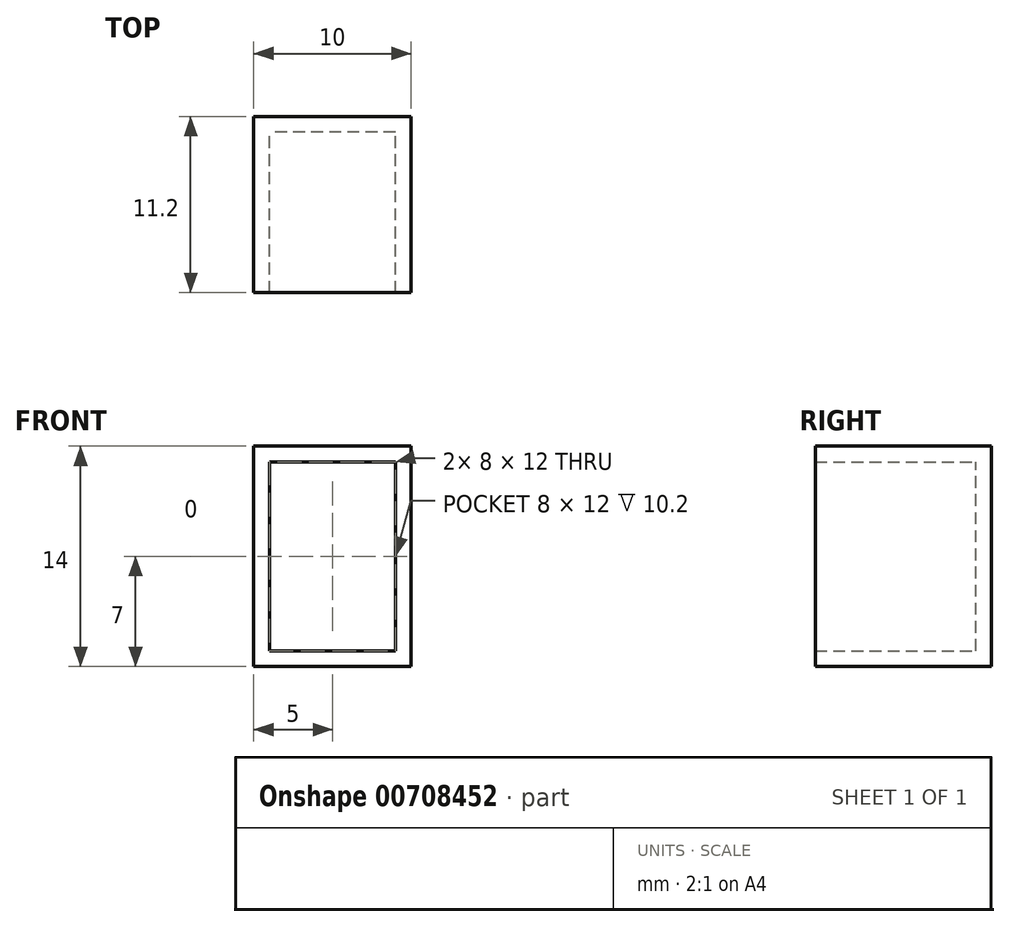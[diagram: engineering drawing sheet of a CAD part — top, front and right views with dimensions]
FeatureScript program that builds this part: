
annotation { "Feature Type Name" : "Feature", "Feature Type Description" : "" }
export const myFeature = defineFeature(function(context is Context, id is Id, definition is map)
    precondition{}
    {
        {
            var Q0;
            Q0=qCreatedBy(makeId("Front.planeOp"),FACE);
            var sketch = newSketch(context, id + "F0", { "sketchPlane" : qUnion([Q0])});
            skLineSegment(sketch, "E0", {"start": v(0, 0) * mm, "end": v(0, 14) * mm});
            skLineSegment(sketch, "E1", {"start": v(0, 14) * mm, "end": v(10, 14) * mm});
            skLineSegment(sketch, "E2", {"start": v(10, 14) * mm, "end": v(10, 0) * mm});
            skLineSegment(sketch, "E3", {"start": v(10, 0) * mm, "end": v(0, 0) * mm});
            skSolve(sketch);
        }
        {
            var Q0;
            Q0 = qSketchRegion(id + "F0", true);
            extrude(context, id + "F1", {"entities" : qUnion([Q0]), "depth" : 11.2 * mm, "offsetDistance" : 25 * mm});
        }
        {
            var Q0;
            Q0=makeQuery(id+"F1.opExtrude","CAP_FACE",FACE,{"disambiguationData":[OSD([sQuery(id+"F0.wireOp",EDGE,"E0"),sQuery(id+"F0.wireOp",EDGE,"E1"),sQuery(id+"F0.wireOp",EDGE,"E2"),sQuery(id+"F0.wireOp",EDGE,"E3")])],"isStart":false});
            shell(context, id + "F2", {"entities" : qUnion([Q0]), "thickness" : 1 * mm});
        }
    });
